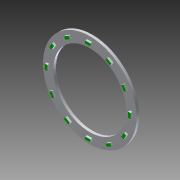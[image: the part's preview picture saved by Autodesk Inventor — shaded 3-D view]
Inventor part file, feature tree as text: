
AUTODESK INVENTOR PART (.ipt)
format: ipt  version: 2014 SP1 (Build 180222100, 222)  size: 162,816 bytes
history: native  units: in
note: dims shown in document units (in); Inventor stores cm internally (conversion verified against a paired STEP export)
features: extrude x2, sketch x1
ambient origin geometry x8: Origin, YZ Plane, XZ Plane, XY Plane, X Axis, Y Axis, Z Axis, Center Point
bodies: Solid1 (feature_tree)
feature tree (3):
  sketch  "Sketch1"  dims[d0=1.75in d1=2.25in d2=0.125in d3=0.0625in d4=4.7244in d6=360.0deg d8=0.0625in d9=0.0in d10=0.05in d11=0.0in]
  extrude  "Extrusion1"  Depth=0.05in
  extrude  "Extrusion2"  Depth=0.125in
